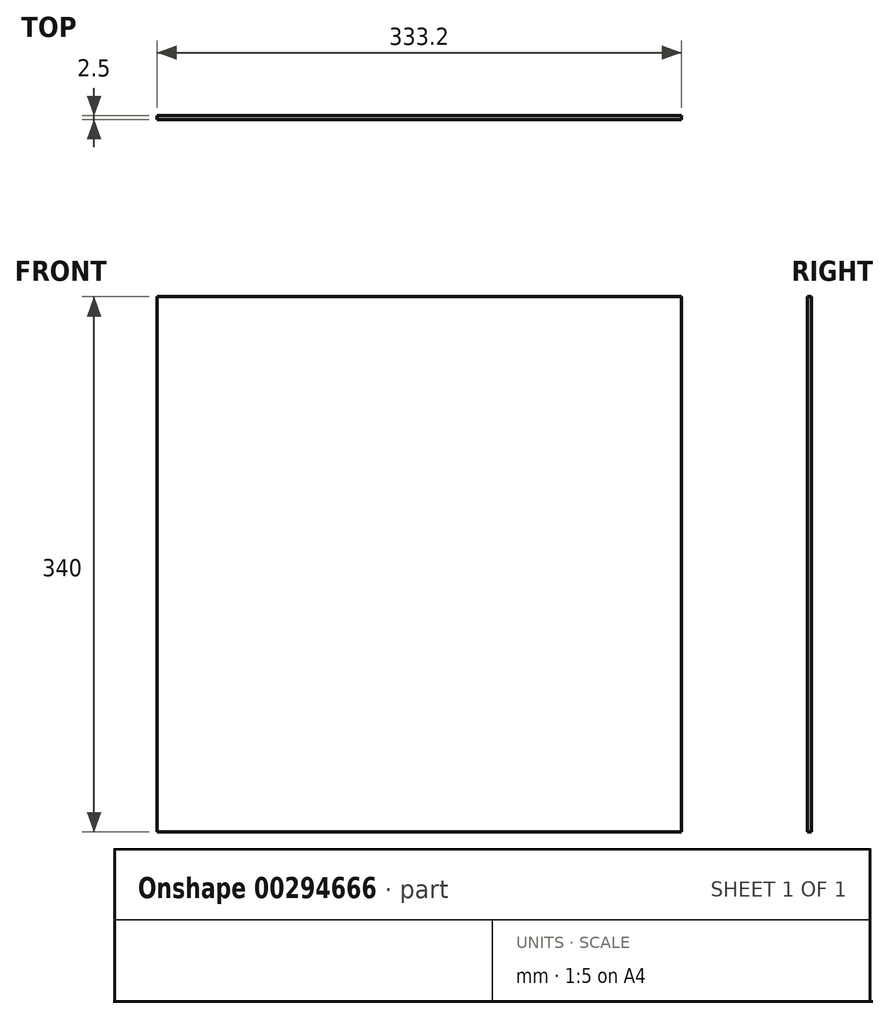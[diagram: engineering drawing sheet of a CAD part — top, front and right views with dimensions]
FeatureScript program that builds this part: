
annotation { "Feature Type Name" : "Feature", "Feature Type Description" : "" }
export const myFeature = defineFeature(function(context is Context, id is Id, definition is map)
    precondition{}
    {
        {
            var Q0;
            Q0=qCreatedBy(makeId("Front.planeOp"),FACE);
            var sketch = newSketch(context, id + "F0", { "sketchPlane" : qUnion([Q0])});
            skLineSegment(sketch, "E0.bottom", {"start": v(-166.6, 170) * mm, "end": v(166.6, 170) * mm});
            skLineSegment(sketch, "E0.top", {"start": v(-166.6, -170) * mm, "end": v(166.6, -170) * mm});
            skLineSegment(sketch, "E0.left", {"start": v(-166.6, 170) * mm, "end": v(-166.6, -170) * mm});
            skLineSegment(sketch, "E0.right", {"start": v(166.6, 170) * mm, "end": v(166.6, -170) * mm});
            skPoint(sketch, "E0.middle", {"position": v(0, 0) * mm});
            skSolve(sketch);
        }
        {
            var Q0;
            Q0=makeQuery(id+"F0.imprint","IMPRINT",FACE,{"disambiguationData":[TD([[makeQuery(id+"F0.imprint","IMPRINT",EDGE,{"derivedFrom":sQuery(id+"F0.wireOp",EDGE,"E0.bottom")}),-1.0]])]});
            extrude(context, id + "F1", {"entities" : qUnion([Q0]), "depth" : 2.5 * mm});
        }
    });
